# Revit family: Lighting - Alva Lidea Wall Sconce
name_source: partatom
category: Lighting Fixtures
units: mm (PartAtom-declared; Revit-internal decimal feet)

## family parameters
Cut with Voids When Loaded = No
Host = Face
Light Source = Yes
Part Type = Normal
Room Calculation Point = No
Round Connector Dimension = Use Diameter
Shared = No

## types (6) — shared parameters
Cap Depth = 0' - 0 7/16"
Color Filter = 16777215
Default Elevation = 4' - 0"
Description = FULLY SEALED HEALTHCARE GRADE LAMP SHADE, HIGH PERFORMANCE LED WALL SCONCE
Dimming Lamp Color Temperature Shift = <None>
Lamp = LED
Light Source Symbol Size = 2' - 0"
Manufacturer = AUBERGE LIGHTING
Type Comments = FULLY SEALED, 120-277V INPUT, ELV/TRIAC DIMMING, 5 YEAR LIMITED WARRANTY, 90 CRI
URL = https://www.alvalight.com

## per-type parameters (varying)
| type | Apparent Load | Emit from Line Length | Height | Lens | Metal | Model | Mounting Location |
| 12" Burano Nickel 2700k | 24 VA | 1' - 0" | 1' - 0" | ALVA Burano | ALVA Eviro Satin Nickel | AU L15W 27 9 SR4W12H B ESN | 0' - 3 1/2" |
| 12" Island Breeze Bronze 3000k | 24 VA | 1' - 0" | 1' - 0" | ALVA Island Breeze | ALVA Enviro Oil-Rubbed Bronze | AU L15W 30 9 SR4W12H IB ESN | 0' - 3 1/2" |
| 12" Gold Shimmer White 3500k | 24 VA | 1' - 0" | 1' - 0" | ALVA Gold Shimmer | ALVA Matt White | AU L15W 35 9 SR4W12H GS WHT | 0' - 3 1/2" |
| 24" White Nickel 2700k | 25 VA | 1' - 11" | 1' - 11" | ALVA White Resin | ALVA Eviro Satin Nickel | AU L30W 27 9 SR4W23H W ESN | 0' - 11 1/2" |
| 34" Autumn Bronze 2700k | 38 VA | 2' - 10" | 2' - 10" | ALVA Autumn | ALVA Enviro Oil-Rubbed Bronze | AU L45W 27 9 SR434H A EOB | 1' - 5" |
| 46" Linear Cross White 3000k | 51 VA | 3' - 9 1/2" | 3' - 9 1/2" | ALVA Linear Cross | ALVA Matt White | AU L60W 30 9 SR4W46H LC WHT | 1' - 10 3/4" |

## geometry (parser evidence)
native form markers: Sweep x5
no freeform markers — native parametric forms only
